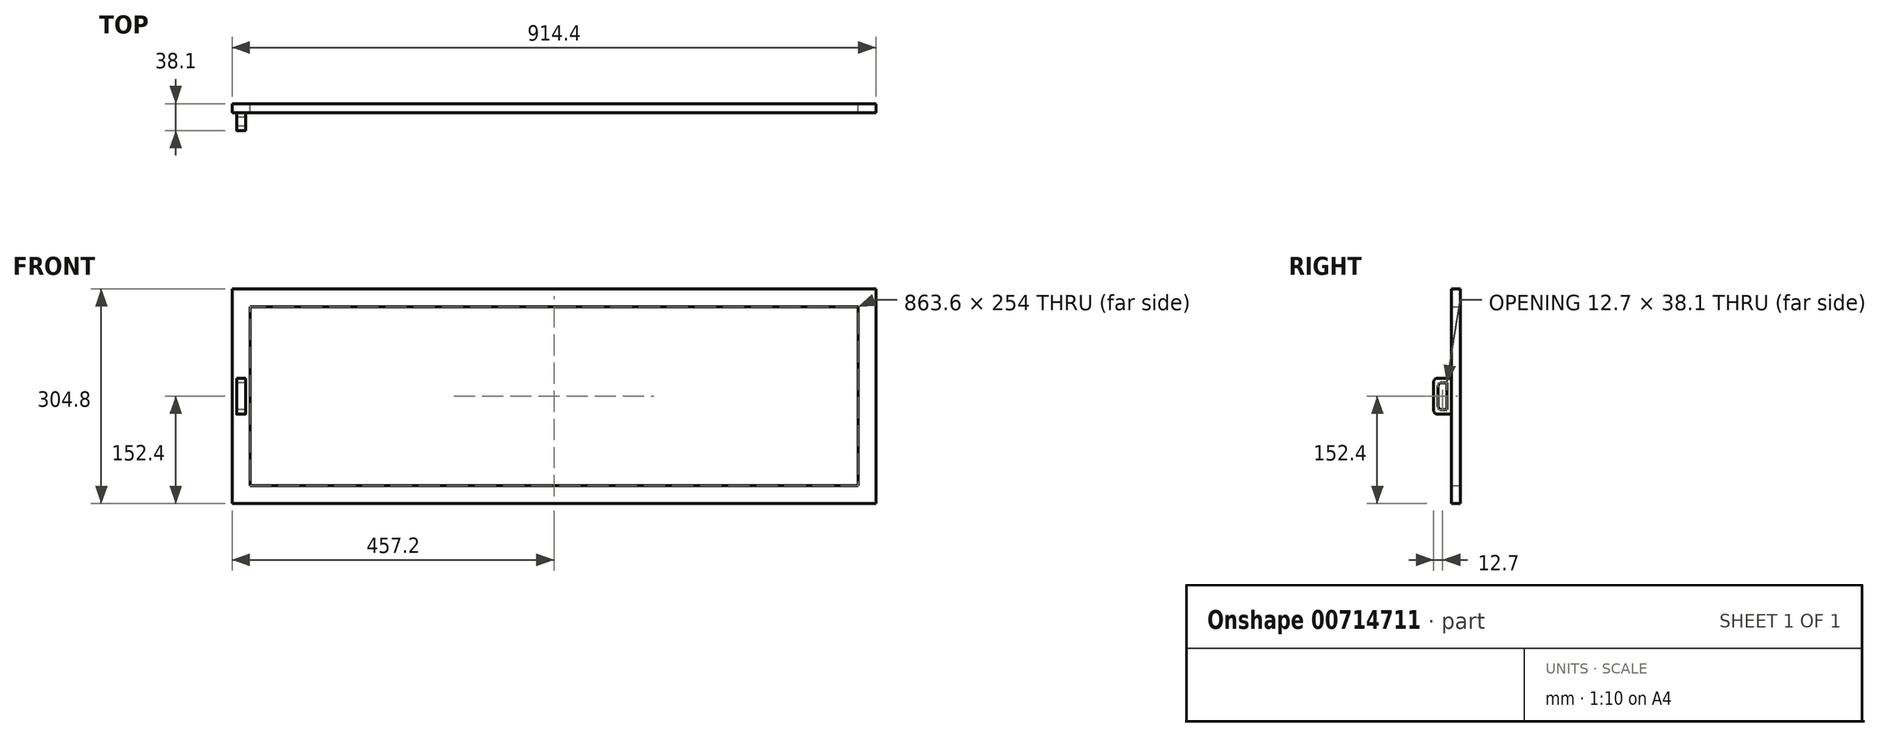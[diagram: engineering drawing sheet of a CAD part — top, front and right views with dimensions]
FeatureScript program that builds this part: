
annotation { "Feature Type Name" : "Feature", "Feature Type Description" : "" }
export const myFeature = defineFeature(function(context is Context, id is Id, definition is map)
    precondition{}
    {
        {
            var Q0;
            Q0=qCreatedBy(makeId("Front.planeOp"),FACE);
            var sketch = newSketch(context, id + "F0", { "sketchPlane" : qUnion([Q0])});
            skLineSegment(sketch, "E0.bottom", {"start": v(457.2, 152.4) * mm, "end": v(-457.2, 152.4) * mm});
            skLineSegment(sketch, "E0.top", {"start": v(457.2, -152.4) * mm, "end": v(-457.2, -152.4) * mm});
            skLineSegment(sketch, "E0.left", {"start": v(457.2, 152.4) * mm, "end": v(457.2, -152.4) * mm});
            skLineSegment(sketch, "E0.right", {"start": v(-457.2, 152.4) * mm, "end": v(-457.2, -152.4) * mm});
            skPoint(sketch, "E0.middle", {"position": v(0, 0) * mm});
            skLineSegment(sketch, "E1.bottom", {"start": v(431.8, 127) * mm, "end": v(-431.8, 127) * mm});
            skLineSegment(sketch, "E1.top", {"start": v(431.8, -127) * mm, "end": v(-431.8, -127) * mm});
            skLineSegment(sketch, "E1.left", {"start": v(431.8, 127) * mm, "end": v(431.8, -127) * mm});
            skLineSegment(sketch, "E1.right", {"start": v(-431.8, 127) * mm, "end": v(-431.8, -127) * mm});
            skSolve(sketch);
        }
        {
            var Q0;
            Q0=makeQuery(id+"F0.imprint","IMPRINT",FACE,{"disambiguationData":[TD([[makeQuery(id+"F0.imprint","IMPRINT",EDGE,{"derivedFrom":sQuery(id+"F0.wireOp",EDGE,"E0.bottom")}),1.0]])]});
            extrude(context, id + "F1", {"entities" : qUnion([Q0]), "endBound" : BoundingType.SYMMETRIC, "depth" : 12.7 * mm, "offsetDistance" : 25.4 * mm});
        }
        {
            var Q0;
            Q0=makeQuery(id+"F1.opExtrude","CAP_FACE",FACE,{"disambiguationData":[OSD([sQuery(id+"F0.wireOp",EDGE,"E0.bottom"),sQuery(id+"F0.wireOp",EDGE,"E0.top"),sQuery(id+"F0.wireOp",EDGE,"E0.left"),sQuery(id+"F0.wireOp",EDGE,"E0.right"),sQuery(id+"F0.wireOp",EDGE,"E1.bottom"),sQuery(id+"F0.wireOp",EDGE,"E1.top"),sQuery(id+"F0.wireOp",EDGE,"E1.left"),sQuery(id+"F0.wireOp",EDGE,"E1.right")])],"isStart":false});
            var sketch = newSketch(context, id + "F2", { "sketchPlane" : qUnion([Q0])});
            skLineSegment(sketch, "E2", {"start": v(-431.8, 0) * mm, "end": v(-444.5, 0) * mm});
            skLineSegment(sketch, "E3.bottom", {"start": v(-438.15, 25.4) * mm, "end": v(-450.85, 25.4) * mm});
            skLineSegment(sketch, "E3.top", {"start": v(-438.15, -25.4) * mm, "end": v(-450.85, -25.4) * mm});
            skLineSegment(sketch, "E3.left", {"start": v(-438.15, 25.4) * mm, "end": v(-438.15, -25.4) * mm});
            skLineSegment(sketch, "E3.right", {"start": v(-450.85, 25.4) * mm, "end": v(-450.85, -25.4) * mm});
            skPoint(sketch, "E3.middle", {"position": v(-444.5, 0) * mm});
            skPoint(sketch, "E3.cornerSnap0", {"position": v(-438.15, 0) * mm});
            skSolve(sketch);
        }
        {
            var Q0;
            Q0 = qSketchRegion(id + "F2", true);
            extrude(context, id + "F3", {"entities" : qUnion([Q0]), "operationType" : NewBodyOperationType.ADD, "depth" : 25.4 * mm, "offsetDistance" : 25.4 * mm});
        }
        {
            var Q0;
            Q0=makeQuery(id+"F3.opExtrude","SWEPT_FACE",FACE,{"disambiguationData":[OSD([sQuery(id+"F2.wireOp",EDGE,"E3.right")])]});
            var sketch = newSketch(context, id + "F4", { "sketchPlane" : qUnion([Q0])});
            skLineSegment(sketch, "E4", {"start": v(31.75, 0) * mm, "end": v(19.05, 0) * mm});
            skLineSegment(sketch, "E5.bottom", {"start": v(25.4, 19.05) * mm, "end": v(12.7, 19.05) * mm});
            skLineSegment(sketch, "E5.top", {"start": v(25.4, -19.05) * mm, "end": v(12.7, -19.05) * mm});
            skLineSegment(sketch, "E5.left", {"start": v(25.4, 19.05) * mm, "end": v(25.4, -19.05) * mm});
            skLineSegment(sketch, "E5.right", {"start": v(12.7, 19.05) * mm, "end": v(12.7, -19.05) * mm});
            skPoint(sketch, "E5.middle", {"position": v(19.05, 0) * mm});
            skPoint(sketch, "E5.cornerSnap0", {"position": v(25.4, 0) * mm});
            skSolve(sketch);
        }
        {
            var Q0;
            Q0 = qSketchRegion(id + "F4", true);
            extrude(context, id + "F5", {"entities" : qUnion([Q0]), "operationType" : NewBodyOperationType.REMOVE, "oppositeDirection" : true, "depth" : 25.4 * mm, "offsetDistance" : 25.4 * mm});
        }
        {
            var Q0;
            Q0=makeQuery(id+"F5.boolean.opBoolean","COPY",EDGE,{"derivedFrom":makeQuery(id+"F5.opExtrude","SWEPT_EDGE",EDGE,{"disambiguationData":[OSD([sQuery(id+"F4.wireOp",EDGE,"E5.bottom"),sQuery(id+"F4.wireOp",EDGE,"E5.left")])]})});
            var Q1;
            Q1=makeQuery(id+"F5.boolean.opBoolean","COPY",EDGE,{"derivedFrom":makeQuery(id+"F5.opExtrude","SWEPT_EDGE",EDGE,{"disambiguationData":[OSD([sQuery(id+"F4.wireOp",EDGE,"E5.top"),sQuery(id+"F4.wireOp",EDGE,"E5.left")])]})});
            fillet(context, id + "F6", {"entities" : qUnion([Q0, Q1]), "radius" : 5.08 * mm, "tangentPropagation" : true, "allowEdgeOverflow" : false});
        }
        {
            var Q0;
            Q0=makeQuery(id+"F3.opExtrude","CAP_EDGE",EDGE,{"disambiguationData":[OSD([sQuery(id+"F2.wireOp",EDGE,"E3.bottom")])],"isStart":false});
            var Q1;
            Q1=makeQuery(id+"F3.opExtrude","CAP_EDGE",EDGE,{"disambiguationData":[OSD([sQuery(id+"F2.wireOp",EDGE,"E3.top")])],"isStart":false});
            fillet(context, id + "F7", {"entities" : qUnion([Q0, Q1]), "radius" : 5.08 * mm, "tangentPropagation" : true, "allowEdgeOverflow" : false});
        }
    });
